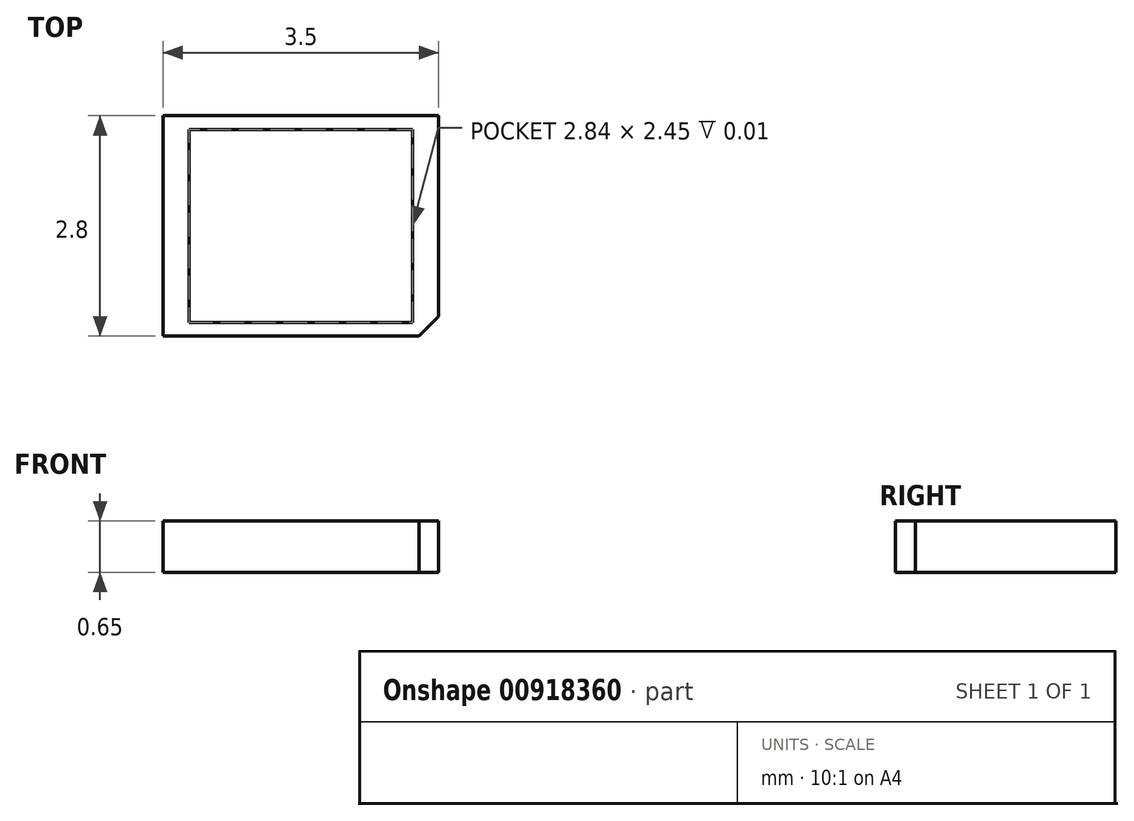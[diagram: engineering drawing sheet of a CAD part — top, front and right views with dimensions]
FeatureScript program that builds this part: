
annotation { "Feature Type Name" : "Feature", "Feature Type Description" : "" }
export const myFeature = defineFeature(function(context is Context, id is Id, definition is map)
    precondition{}
    {
        {
            var Q0;
            Q0=qCreatedBy(makeId("Top.planeOp"),FACE);
            var sketch = newSketch(context, id + "F0", { "sketchPlane" : qUnion([Q0])});
            skLineSegment(sketch, "E0.bottom", {"start": v(3.5, 2.8) * mm, "end": v(0, 2.8) * mm});
            skLineSegment(sketch, "E0.top", {"start": v(3.5, 0) * mm, "end": v(0, 0) * mm});
            skLineSegment(sketch, "E0.left", {"start": v(3.5, 2.8) * mm, "end": v(3.5, 0) * mm});
            skLineSegment(sketch, "E0.right", {"start": v(0, 2.8) * mm, "end": v(0, 0) * mm});
            skSolve(sketch);
        }
        {
            var Q0;
            Q0 = qSketchRegion(id + "F0", true);
            extrude(context, id + "F1", {"entities" : qUnion([Q0]), "oppositeDirection" : true, "depth" : 0.65 * mm, "offsetDistance" : 25.4 * mm});
        }
        {
            var Q0;
            Q0=makeQuery(id+"F1.opExtrude","CAP_FACE",FACE,{"disambiguationData":[OSD([sQuery(id+"F0.wireOp",EDGE,"E0.bottom"),sQuery(id+"F0.wireOp",EDGE,"E0.top"),sQuery(id+"F0.wireOp",EDGE,"E0.left"),sQuery(id+"F0.wireOp",EDGE,"E0.right")])],"isStart":true});
            var sketch = newSketch(context, id + "F2", { "sketchPlane" : qUnion([Q0])});
            skLineSegment(sketch, "E1.bottom", {"start": v(0.33, 0.17) * mm, "end": v(3.17, 0.17) * mm});
            skLineSegment(sketch, "E1.top", {"start": v(0.33, 2.62) * mm, "end": v(3.17, 2.62) * mm});
            skLineSegment(sketch, "E1.left", {"start": v(0.33, 0.17) * mm, "end": v(0.33, 2.63) * mm});
            skLineSegment(sketch, "E1.right", {"start": v(3.17, 0.18) * mm, "end": v(3.17, 2.63) * mm});
            skSolve(sketch);
        }
        {
            var Q0;
            Q0 = qSketchRegion(id + "F2", true);
            extrude(context, id + "F3", {"entities" : qUnion([Q0]), "operationType" : NewBodyOperationType.REMOVE, "oppositeDirection" : true, "depth" : 0.01 * mm, "offsetDistance" : 25.4 * mm});
        }
        {
            var Q0;
            Q0=makeQuery(id+"F1.opExtrude","SWEPT_EDGE",EDGE,{"disambiguationData":[OSD([sQuery(id+"F0.wireOp",EDGE,"E0.top"),sQuery(id+"F0.wireOp",EDGE,"E0.left")])]});
            chamfer(context, id + "F4", {"entities" : qUnion([Q0]), "width" : 0.25 * mm, "tangentPropagation" : true});
        }
    });
